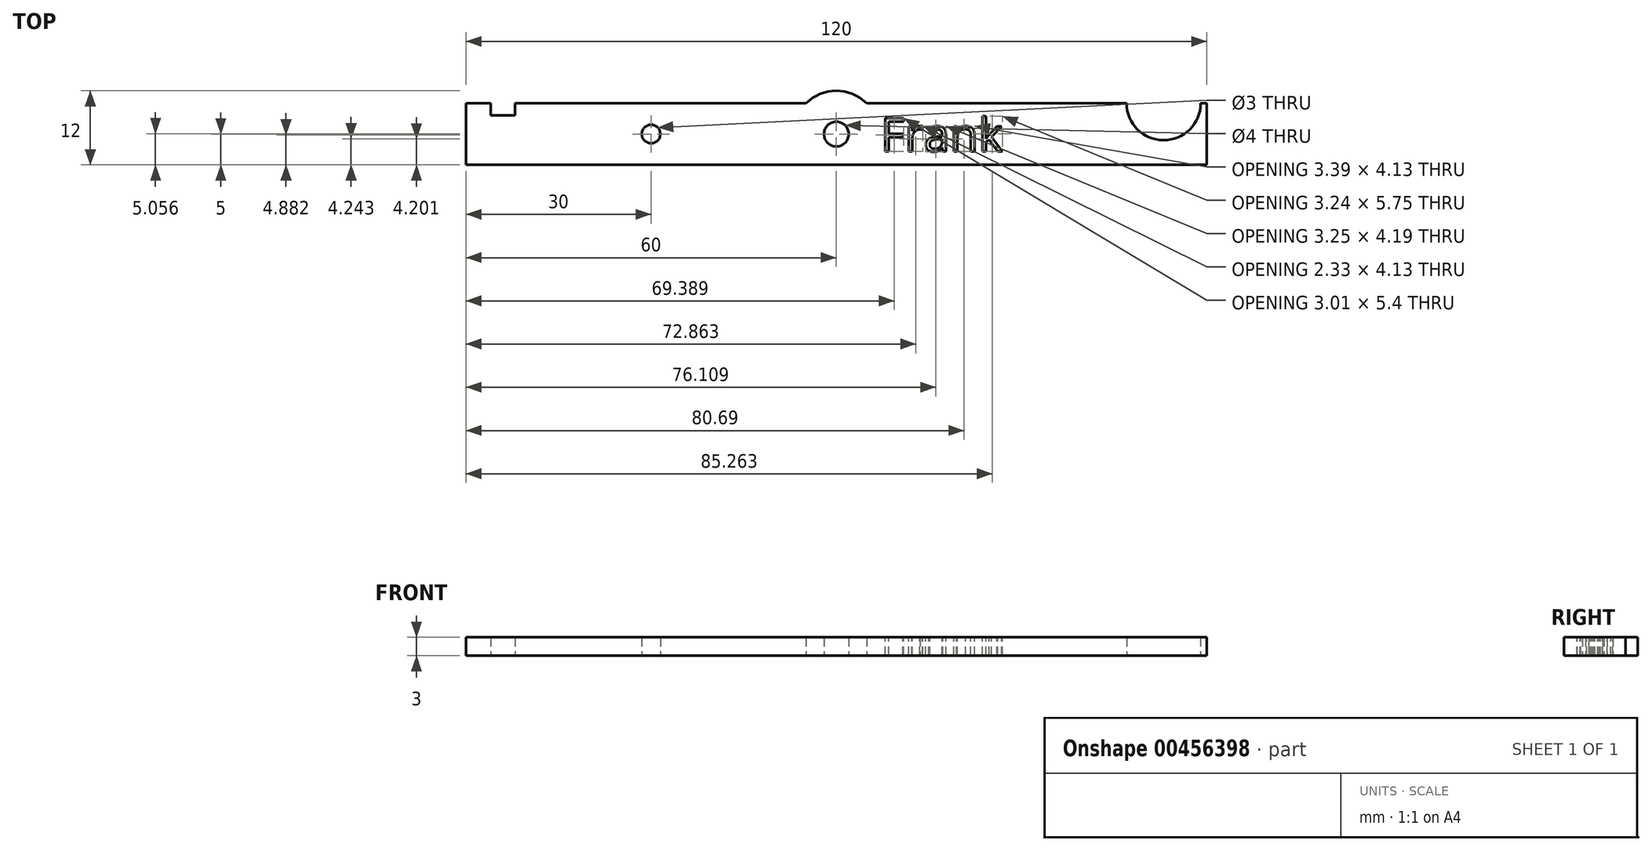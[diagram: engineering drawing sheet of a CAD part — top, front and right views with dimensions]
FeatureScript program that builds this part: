
annotation { "Feature Type Name" : "Feature", "Feature Type Description" : "" }
export const myFeature = defineFeature(function(context is Context, id is Id, definition is map)
    precondition{}
    {
        {
            var Q0;
            Q0=qCreatedBy(makeId("Top.planeOp"),FACE);
            var sketch = newSketch(context, id + "F0", { "sketchPlane" : qUnion([Q0])});
            skLineSegment(sketch, "E0.bottom", {"start": v(-60, -5) * mm, "end": v(60, -5) * mm});
            skLineSegment(sketch, "E0.top", {"start": v(-60, 5) * mm, "end": v(60, 5) * mm});
            skLineSegment(sketch, "E0.left", {"start": v(-60, -5) * mm, "end": v(-60, 5) * mm});
            skLineSegment(sketch, "E0.right", {"start": v(60, -5) * mm, "end": v(60, 5) * mm});
            skPoint(sketch, "E0.middle", {"position": v(0, 0) * mm});
            skLineSegment(sketch, "E1.bottom", {"start": v(-52, 5) * mm, "end": v(-56, 5) * mm});
            skLineSegment(sketch, "E1.top", {"start": v(-52, 3) * mm, "end": v(-56, 3) * mm});
            skLineSegment(sketch, "E1.left", {"start": v(-52, 5) * mm, "end": v(-52, 3) * mm});
            skLineSegment(sketch, "E1.right", {"start": v(-56, 5) * mm, "end": v(-56, 3) * mm});
            skCircle(sketch, "E2", {"center": v(0, 0) * mm, "radius": 2 * mm});
            skCircle(sketch, "E3", {"center": v(0, 0) * mm, "radius": 7 * mm});
            skCircle(sketch, "E4", {"center": v(53, 5) * mm, "radius": 6 * mm});
            skCircle(sketch, "E5", {"center": v(-30, 0) * mm, "radius": 1.5 * mm});
            skSolve(sketch);
        }
        {
            var Q0;
            {var subQ0=sQuery(id+"F0.wireOp",EDGE,"E0.left");Q0=makeQuery(id+"F0.imprint","IMPRINT",FACE,{"disambiguationData":[TD([[makeQuery(id+"F0.imprint","IMPRINT",EDGE,{"derivedFrom":subQ0}),-1.0]])]});}
            var Q1;
            {var subQ0=sQuery(id+"F0.wireOp",EDGE,"E0.right");Q1=makeQuery(id+"F0.imprint","IMPRINT",FACE,{"disambiguationData":[TD([[makeQuery(id+"F0.imprint","IMPRINT",EDGE,{"derivedFrom":subQ0}),1.0]])]});}
            var Q2;
            {var subQ0=sQuery(id+"F0.wireOp",EDGE,"E3");var subQ1=sQuery(id+"F0.wireOp",EDGE,"E0.bottom");var subQ2=makeQuery(id+"F0.imprint","INTERSECT",VERTEX,{"disambiguationData":[OD(0.0)],"derivedFrom":[subQ1,subQ0]});Q2=makeQuery(id+"F0.imprint","IMPRINT",FACE,{"disambiguationData":[TD([[makeQuery(id+"F0.imprint","IMPRINT",EDGE,{"disambiguationData":[TD([[subQ2,-1.0]])],"derivedFrom":subQ1}),-1.0]])]});}
            var Q3;
            Q3=makeQuery(id+"F0.imprint","IMPRINT",FACE,{"disambiguationData":[TD([[makeQuery(id+"F0.imprint","IMPRINT",EDGE,{"derivedFrom":sQuery(id+"F0.wireOp",EDGE,"E2")}),-1.0]])]});
            var Q4;
            {var subQ0=sQuery(id+"F0.wireOp",EDGE,"E3");var subQ1=sQuery(id+"F0.wireOp",EDGE,"E0.top");var subQ2=makeQuery(id+"F0.imprint","INTERSECT",VERTEX,{"disambiguationData":[OD(0.0)],"derivedFrom":[subQ1,subQ0]});Q4=makeQuery(id+"F0.imprint","IMPRINT",FACE,{"disambiguationData":[TD([[makeQuery(id+"F0.imprint","IMPRINT",EDGE,{"disambiguationData":[TD([[subQ2,-1.0]])],"derivedFrom":subQ1}),1.0]])]});}
            extrude(context, id + "F1", {"entities" : qUnion([Q0, Q1, Q2, Q3, Q4]), "depth" : 3 * mm});
        }
        {
            var Q0;
            Q0=makeQuery(id+"F1.opExtrude","CAP_FACE",FACE,{"disambiguationData":[OSD([sQuery(id+"F0.wireOp",EDGE,"E0.bottom"),sQuery(id+"F0.wireOp",EDGE,"E0.top"),sQuery(id+"F0.wireOp",EDGE,"E0.left"),sQuery(id+"F0.wireOp",EDGE,"E0.right"),sQuery(id+"F0.wireOp",EDGE,"E1.top"),sQuery(id+"F0.wireOp",EDGE,"E1.left"),sQuery(id+"F0.wireOp",EDGE,"E1.right"),sQuery(id+"F0.wireOp",EDGE,"E2"),sQuery(id+"F0.wireOp",EDGE,"E3"),sQuery(id+"F0.wireOp",EDGE,"E4"),sQuery(id+"F0.wireOp",EDGE,"E5")])],"isStart":false});
            var sketch = newSketch(context, id + "F2", { "sketchPlane" : qUnion([Q0])});
            skText(sketch, "E6", { "text": "Frank\n", "fontName": "OpenSans-Regular.ttf"});
            const initialGuessF2  = {"E6": [0.00714, -0.00282, 1, 0, 0.00545]};
            skSetInitialGuess(sketch, initialGuessF2);
            skSolve(sketch);
        }
        {
            var Q0;
            Q0=makeQuery(id+"F2.imprint","IMPRINT",FACE,{"disambiguationData":[TD([[makeQuery(id+"F2.imprint","IMPRINT",EDGE,{"derivedFrom":sQuery(id+"F2.wireOp",EDGE,"E6.sketch_text.stroke-0")}),-1.0]])]});
            var Q1;
            Q1=makeQuery(id+"F2.imprint","IMPRINT",FACE,{"disambiguationData":[TD([[makeQuery(id+"F2.imprint","IMPRINT",EDGE,{"derivedFrom":sQuery(id+"F2.wireOp",EDGE,"E6.sketch_text.stroke-10")}),-1.0]])]});
            var Q2;
            Q2=makeQuery(id+"F2.imprint","IMPRINT",FACE,{"disambiguationData":[TD([[makeQuery(id+"F2.imprint","IMPRINT",EDGE,{"derivedFrom":sQuery(id+"F2.wireOp",EDGE,"E6.sketch_text.stroke-23")}),-1.0]])]});
            var Q3;
            Q3=makeQuery(id+"F2.imprint","IMPRINT",FACE,{"disambiguationData":[TD([[makeQuery(id+"F2.imprint","IMPRINT",EDGE,{"derivedFrom":sQuery(id+"F2.wireOp",EDGE,"E6.sketch_text.stroke-50")}),-1.0]])]});
            var Q4;
            Q4=makeQuery(id+"F2.imprint","IMPRINT",FACE,{"disambiguationData":[TD([[makeQuery(id+"F2.imprint","IMPRINT",EDGE,{"derivedFrom":sQuery(id+"F2.wireOp",EDGE,"E6.sketch_text.stroke-67")}),-1.0]])]});
            extrude(context, id + "F3", {"entities" : qUnion([Q0, Q1, Q2, Q3, Q4]), "operationType" : NewBodyOperationType.REMOVE, "oppositeDirection" : true, "depth" : 25 * mm});
        }
    });
